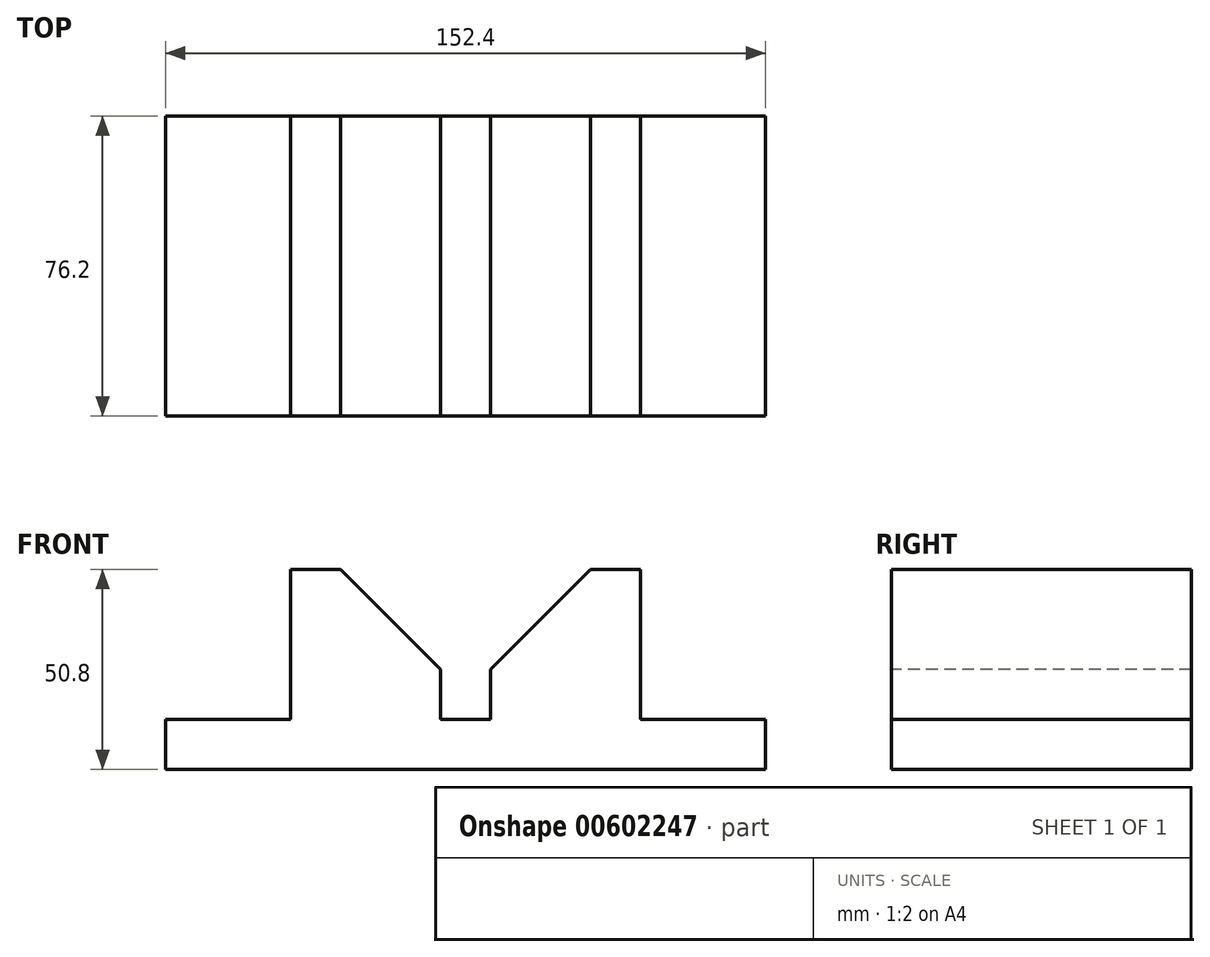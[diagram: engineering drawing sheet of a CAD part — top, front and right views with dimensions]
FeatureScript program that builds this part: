
annotation { "Feature Type Name" : "Feature", "Feature Type Description" : "" }
export const myFeature = defineFeature(function(context is Context, id is Id, definition is map)
    precondition{}
    {
        {
            var Q0;
            Q0=qCreatedBy(makeId("Front.planeOp"),FACE);
            var sketch = newSketch(context, id + "F0", { "sketchPlane" : qUnion([Q0])});
            skLineSegment(sketch, "E0.top", {"start": v(0, 50.8) * mm, "end": v(152.4, 50.8) * mm});
            skLineSegment(sketch, "E0.left", {"start": v(0, 0) * mm, "end": v(0, 50.8) * mm});
            skLineSegment(sketch, "E0.right", {"start": v(152.4, 0) * mm, "end": v(152.4, 50.8) * mm});
            skLineSegment(sketch, "E1", {"start": v(0, 0) * mm, "end": v(152.4, 0) * mm});
            skSolve(sketch);
        }
        {
            var Q0;
            Q0=makeQuery(id+"F0.imprint","IMPRINT",FACE,{"disambiguationData":[TD([[makeQuery(id+"F0.imprint","IMPRINT",EDGE,{"derivedFrom":sQuery(id+"F0.wireOp",EDGE,"E0.top")}),-1.0]])]});
            extrude(context, id + "F1", {"entities" : qUnion([Q0]), "depth" : 76.2 * mm, "offsetDistance" : 25.4 * mm});
        }
        {
            var Q0;
            Q0=makeQuery(id+"F1.opExtrude","CAP_FACE",FACE,{"disambiguationData":[OSD([sQuery(id+"F0.wireOp",EDGE,"E0.top"),sQuery(id+"F0.wireOp",EDGE,"E0.left"),sQuery(id+"F0.wireOp",EDGE,"E0.right"),sQuery(id+"F0.wireOp",EDGE,"E1")])],"isStart":false});
            var sketch = newSketch(context, id + "F2", { "sketchPlane" : qUnion([Q0])});
            skLineSegment(sketch, "E2", {"start": v(120.65, 50.8) * mm, "end": v(120.65, 12.7) * mm});
            skLineSegment(sketch, "E3", {"start": v(120.65, 12.7) * mm, "end": v(152.4, 12.7) * mm});
            skLineSegment(sketch, "E4", {"start": v(0, 12.7) * mm, "end": v(31.75, 12.7) * mm});
            skLineSegment(sketch, "E5", {"start": v(31.75, 12.7) * mm, "end": v(31.75, 50.8) * mm});
            skSolve(sketch);
        }
        {
            var Q0;
            Q0 = qSketchRegion(id + "F2", true);
            var Q1;
            {var subQ0=sQuery(id+"F2.wireOp",EDGE,"E4");Q1=makeQuery(id+"F2.imprint","IMPRINT",FACE,{"disambiguationData":[TD([[makeQuery(id+"F2.imprint","IMPRINT",EDGE,{"derivedFrom":subQ0}),1.0]])]});}
            var Q2;
            {var subQ0=sQuery(id+"F2.wireOp",EDGE,"E2");Q2=makeQuery(id+"F2.imprint","IMPRINT",FACE,{"disambiguationData":[TD([[makeQuery(id+"F2.imprint","IMPRINT",EDGE,{"derivedFrom":subQ0}),1.0]])]});}
            extrude(context, id + "F3", {"entities" : qUnion([Q0, Q1, Q2]), "operationType" : NewBodyOperationType.REMOVE, "oppositeDirection" : true, "depth" : 2540 * mm, "offsetDistance" : 25.4 * mm});
        }
        {
            var Q0;
            Q0=makeQuery(id+"F1.opExtrude","CAP_FACE",FACE,{"disambiguationData":[OSD([sQuery(id+"F0.wireOp",EDGE,"E0.top"),sQuery(id+"F0.wireOp",EDGE,"E0.left"),sQuery(id+"F0.wireOp",EDGE,"E0.right"),sQuery(id+"F0.wireOp",EDGE,"E1")])],"isStart":false});
            var sketch = newSketch(context, id + "F4", { "sketchPlane" : qUnion([Q0])});
            skLineSegment(sketch, "E6", {"start": v(76.2, 12.7) * mm, "end": v(69.85, 12.7) * mm});
            skLineSegment(sketch, "E7", {"start": v(76.2, 12.7) * mm, "end": v(82.55, 12.7) * mm});
            skLineSegment(sketch, "E8", {"start": v(69.85, 12.7) * mm, "end": v(69.85, 25.4) * mm});
            skLineSegment(sketch, "E9", {"start": v(82.55, 12.7) * mm, "end": v(82.55, 25.4) * mm});
            skLineSegment(sketch, "E10", {"start": v(31.75, 50.8) * mm, "end": v(44.45, 50.8) * mm});
            skLineSegment(sketch, "E11", {"start": v(120.65, 50.8) * mm, "end": v(107.95, 50.8) * mm});
            skLineSegment(sketch, "E12", {"start": v(82.55, 25.4) * mm, "end": v(107.95, 50.8) * mm});
            skLineSegment(sketch, "E13", {"start": v(69.85, 25.4) * mm, "end": v(44.45, 50.8) * mm});
            skSolve(sketch);
        }
        {
            var Q0;
            Q0=makeQuery(id+"F4.imprint","IMPRINT",FACE,{"disambiguationData":[TD([[makeQuery(id+"F4.imprint","IMPRINT",EDGE,{"derivedFrom":sQuery(id+"F4.wireOp",EDGE,"E6")}),-1.0]])]});
            extrude(context, id + "F5", {"entities" : qUnion([Q0]), "operationType" : NewBodyOperationType.REMOVE, "oppositeDirection" : true, "depth" : 254 * mm, "offsetDistance" : 25.4 * mm});
        }
    });
